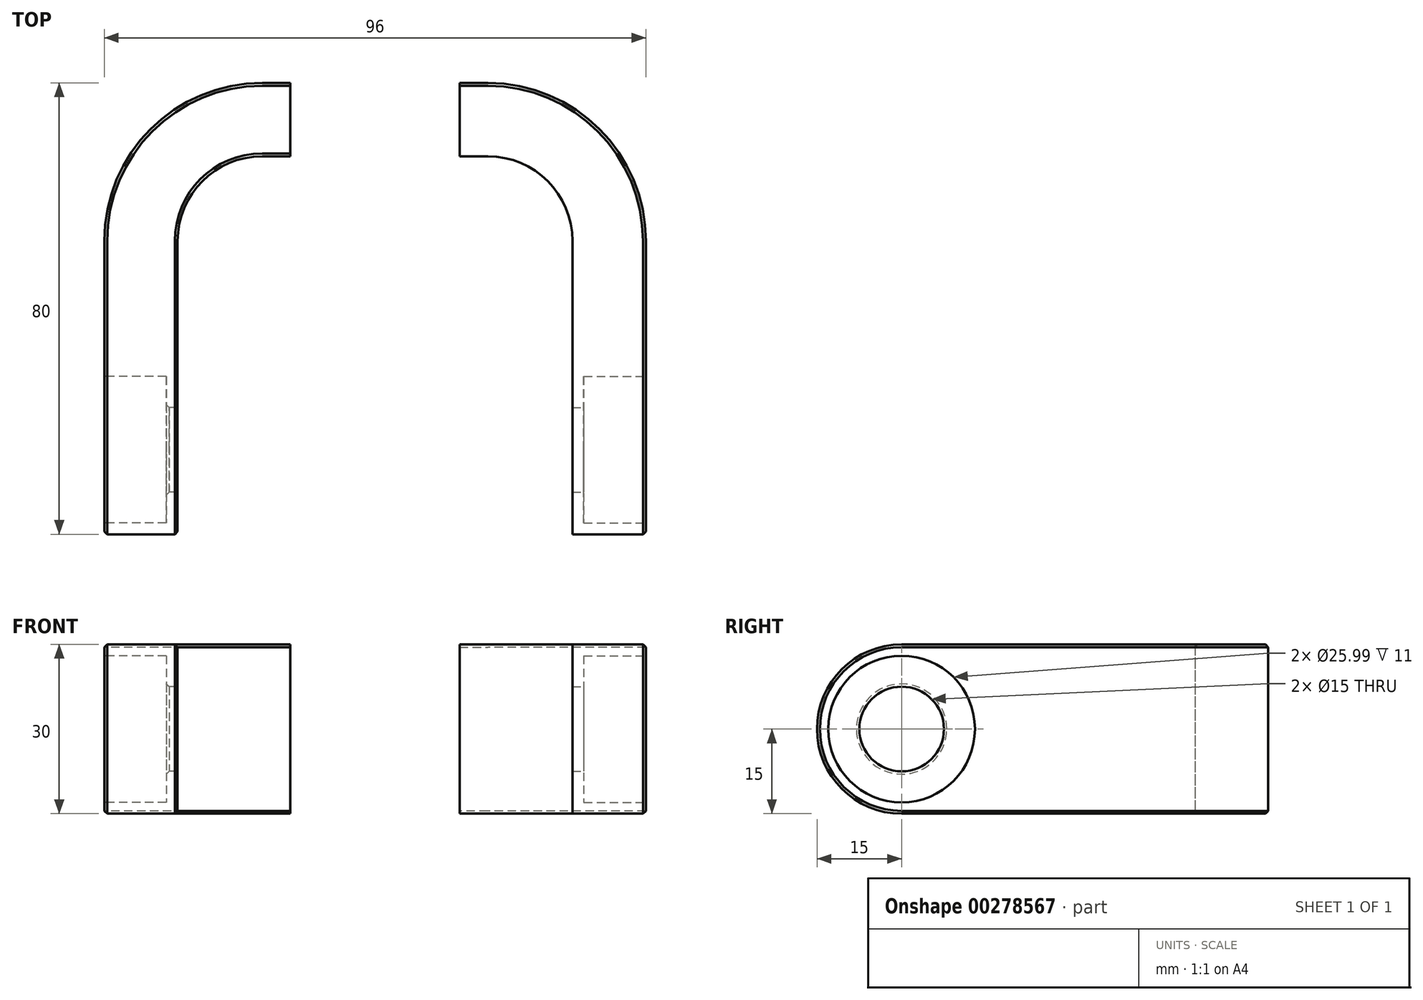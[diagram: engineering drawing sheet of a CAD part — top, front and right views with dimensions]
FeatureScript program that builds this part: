
annotation { "Feature Type Name" : "Feature", "Feature Type Description" : "" }
export const myFeature = defineFeature(function(context is Context, id is Id, definition is map)
    precondition{}
    {
        {
            var Q0;
            Q0=qCreatedBy(makeId("Top.planeOp"),FACE);
            var sketch = newSketch(context, id + "F0", { "sketchPlane" : qUnion([Q0])});
            skLineSegment(sketch, "E0.bottom", {"start": v(35, -52) * mm, "end": v(-35, -52) * mm});
            skLineSegment(sketch, "E0.top", {"start": v(35, 52) * mm, "end": v(-35, 52) * mm});
            skLineSegment(sketch, "E0.left", {"start": v(35, -52) * mm, "end": v(35, 52) * mm});
            skLineSegment(sketch, "E0.right", {"start": v(-35, -52) * mm, "end": v(-35, 52) * mm});
            skPoint(sketch, "E0.middle", {"position": v(0, 0) * mm});
            skLineSegment(sketch, "E1.bottom", {"start": v(48, -65) * mm, "end": v(-48, -65) * mm});
            skLineSegment(sketch, "E1.top", {"start": v(48, 65) * mm, "end": v(-48, 65) * mm});
            skLineSegment(sketch, "E1.left", {"start": v(48, -65) * mm, "end": v(48, 65) * mm});
            skLineSegment(sketch, "E1.right", {"start": v(-48, -65) * mm, "end": v(-48, 65) * mm});
            skLineSegment(sketch, "E2", {"start": v(-48, 0) * mm, "end": v(0, 0) * mm, "construction": true});
            skLineSegment(sketch, "E3", {"start": v(48, 0) * mm, "end": v(0, 0) * mm, "construction": true});
            skLineSegment(sketch, "E4", {"start": v(0, 65) * mm, "end": v(0, -65) * mm, "construction": true});
            skLineSegment(sketch, "E5.bottom", {"start": v(-35, 15) * mm, "end": v(-48, 15) * mm});
            skLineSegment(sketch, "E5.top", {"start": v(-35, -15) * mm, "end": v(-48, -15) * mm});
            skLineSegment(sketch, "E5.left", {"start": v(-35, 15) * mm, "end": v(-35, -15) * mm});
            skLineSegment(sketch, "E5.right", {"start": v(-48, 15) * mm, "end": v(-48, -15) * mm});
            skPoint(sketch, "E5.middle", {"position": v(-41.5, 0) * mm});
            skLineSegment(sketch, "E6.bottom", {"start": v(48, 15) * mm, "end": v(35, 15) * mm});
            skLineSegment(sketch, "E6.top", {"start": v(48, -15) * mm, "end": v(35, -15) * mm});
            skLineSegment(sketch, "E6.left", {"start": v(48, 15) * mm, "end": v(48, -15) * mm});
            skLineSegment(sketch, "E6.right", {"start": v(35, 15) * mm, "end": v(35, -15) * mm});
            skPoint(sketch, "E6.middle", {"position": v(41.5, 0) * mm});
            skLineSegment(sketch, "E7.bottom", {"start": v(15, 65) * mm, "end": v(-15, 65) * mm});
            skLineSegment(sketch, "E7.top", {"start": v(15, 52) * mm, "end": v(-15, 52) * mm});
            skLineSegment(sketch, "E7.left", {"start": v(15, 65) * mm, "end": v(15, 52) * mm});
            skLineSegment(sketch, "E7.right", {"start": v(-15, 65) * mm, "end": v(-15, 52) * mm});
            skPoint(sketch, "E7.middle", {"position": v(0, 58.5) * mm});
            skSolve(sketch);
        }
        {
            var Q0;
            Q0=makeQuery(id+"F0.imprint","IMPRINT",FACE,{"disambiguationData":[TD([[makeQuery(id+"F0.imprint","IMPRINT",EDGE,{"derivedFrom":sQuery(id+"F0.wireOp",EDGE,"E7.bottom")}),1.0]])]});
            var Q1;
            {var subQ3=sQuery(id+"F0.wireOp",EDGE,"E5.bottom");Q1=makeQuery(id+"F0.imprint","IMPRINT",FACE,{"disambiguationData":[TD([[makeQuery(id+"F0.imprint","IMPRINT",EDGE,{"derivedFrom":subQ3}),-1.0]])]});}
            var Q2;
            Q2=makeQuery(id+"F0.imprint","IMPRINT",FACE,{"disambiguationData":[TD([[makeQuery(id+"F0.imprint","IMPRINT",EDGE,{"derivedFrom":sQuery(id+"F0.wireOp",EDGE,"E5.bottom")}),1.0]])]});
            var Q3;
            {var subQ7=sQuery(id+"F0.wireOp",EDGE,"E6.bottom");Q3=makeQuery(id+"F0.imprint","IMPRINT",FACE,{"disambiguationData":[TD([[makeQuery(id+"F0.imprint","IMPRINT",EDGE,{"derivedFrom":subQ7}),-1.0]])]});}
            var Q4;
            Q4=makeQuery(id+"F0.imprint","IMPRINT",FACE,{"disambiguationData":[TD([[makeQuery(id+"F0.imprint","IMPRINT",EDGE,{"derivedFrom":sQuery(id+"F0.wireOp",EDGE,"E6.bottom")}),1.0]])]});
            extrude(context, id + "F1", {"entities" : qUnion([Q0, Q1, Q2, Q3, Q4]), "depth" : 15 * mm, "hasSecondDirection" : true, "secondDirectionOppositeDirection" : true, "secondDirectionDepth" : 15 * mm});
        }
        {
            var Q0;
            Q0=makeQuery(id+"F1.opExtrude","CAP_EDGE",EDGE,{"disambiguationData":[OSD([sQuery(id+"F0.wireOp",EDGE,"E5.top")])],"isStart":false});
            var Q1;
            Q1=makeQuery(id+"F1.opExtrude","CAP_EDGE",EDGE,{"disambiguationData":[OSD([sQuery(id+"F0.wireOp",EDGE,"E5.top")])],"isStart":true});
            var Q2;
            Q2=makeQuery(id+"F1.opExtrude","CAP_EDGE",EDGE,{"disambiguationData":[OSD([sQuery(id+"F0.wireOp",EDGE,"E6.top")])],"isStart":false});
            var Q3;
            Q3=makeQuery(id+"F1.opExtrude","CAP_EDGE",EDGE,{"disambiguationData":[OSD([sQuery(id+"F0.wireOp",EDGE,"E6.top")])],"isStart":true});
            var Q4;
            Q4=makeQuery(id+"F1.opExtrude","SWEPT_EDGE",EDGE,{"disambiguationData":[OSD([sQuery(id+"F0.wireOp",EDGE,"E0.top"),sQuery(id+"F0.wireOp",EDGE,"E0.right")])]});
            var Q5;
            Q5=makeQuery(id+"F1.opExtrude","SWEPT_EDGE",EDGE,{"disambiguationData":[OSD([sQuery(id+"F0.wireOp",EDGE,"E0.top"),sQuery(id+"F0.wireOp",EDGE,"E0.left")])]});
            var Q6;
            Q6=makeQuery(id+"FhP4Di1fzt5Cq4O_0.boolean.opBoolean","COPY",FACE,{"derivedFrom":makeQuery(id+"FhP4Di1fzt5Cq4O_0.opExtrude","SWEPT_FACE",FACE,{"disambiguationData":[OSD([sQuery(id+"F0.wireOp",EDGE,"E7.right")])]})});
            var Q7;
            Q7=makeQuery(id+"FhP4Di1fzt5Cq4O_0.boolean.opBoolean","COPY",EDGE,{"derivedFrom":makeQuery(id+"FhP4Di1fzt5Cq4O_0.opExtrude","CAP_EDGE",EDGE,{"disambiguationData":[OSD([sQuery(id+"F0.wireOp",EDGE,"E7.right")])],"isStart":false})});
            fillet(context, id + "F2", {"entities" : qUnion([Q0, Q1, Q2, Q3, Q4, Q5, Q6, Q7]), "radius" : 15 * mm, "tangentPropagation" : true, "allowEdgeOverflow" : false});
        }
        {
            var Q0;
            Q0=makeQuery(id+"F1.opExtrude","SWEPT_EDGE",EDGE,{"disambiguationData":[OSD([sQuery(id+"F0.wireOp",EDGE,"E1.top"),sQuery(id+"F0.wireOp",EDGE,"E1.left")])]});
            var Q1;
            Q1=makeQuery(id+"F1.opExtrude","SWEPT_EDGE",EDGE,{"disambiguationData":[OSD([sQuery(id+"F0.wireOp",EDGE,"E1.top"),sQuery(id+"F0.wireOp",EDGE,"E1.right")])]});
            fillet(context, id + "F3", {"entities" : qUnion([Q0, Q1]), "radius" : 28 * mm, "tangentPropagation" : true, "allowEdgeOverflow" : false});
        }
        {
            var Q0;
            Q0=makeQuery(id+"F1.opExtrude","SWEPT_FACE",FACE,{"disambiguationData":[OSD([sQuery(id+"F0.wireOp",EDGE,"E1.right"),sQuery(id+"F0.wireOp",EDGE,"E5.right")])]});
            var sketch = newSketch(context, id + "F4", { "sketchPlane" : qUnion([Q0])});
            skCircle(sketch, "E8", {"center": v(0, 0) * mm, "radius": 13 * mm});
            skCircle(sketch, "E9", {"center": v(0, 0) * mm, "radius": 7.5 * mm});
            skSolve(sketch);
        }
        {
            var Q0;
            Q0=makeQuery(id+"F4.imprint","IMPRINT",FACE,{"disambiguationData":[TD([[makeQuery(id+"F4.imprint","IMPRINT",EDGE,{"derivedFrom":sQuery(id+"F4.wireOp",EDGE,"E8")}),1.0]])]});
            var Q1;
            Q1=makeQuery(id+"F4.imprint","IMPRINT",FACE,{"disambiguationData":[TD([[makeQuery(id+"F4.imprint","IMPRINT",EDGE,{"derivedFrom":sQuery(id+"F4.wireOp",EDGE,"E9")}),1.0]])]});
            extrude(context, id + "F5", {"entities" : qUnion([Q0, Q1]), "operationType" : NewBodyOperationType.REMOVE, "oppositeDirection" : true, "depth" : 11 * mm});
        }
        {
            var Q0;
            Q0=makeQuery(id+"F4.imprint","IMPRINT",FACE,{"disambiguationData":[TD([[makeQuery(id+"F4.imprint","IMPRINT",EDGE,{"derivedFrom":sQuery(id+"F4.wireOp",EDGE,"E9")}),1.0]])]});
            var Q1;
            Q1=sQuery(id+"F4.wireOp",EDGE,"E9");
            extrude(context, id + "F6", {"entities" : qUnion([Q0]), "operationType" : NewBodyOperationType.REMOVE, "surfaceEntities" : qUnion([Q1]), "oppositeDirection" : true, "depth" : 13 * mm});
        }
        {
            var Q0;
            Q0=makeQuery(id+"F1.opExtrude","SWEPT_FACE",FACE,{"disambiguationData":[OSD([sQuery(id+"F0.wireOp",EDGE,"E1.top"),sQuery(id+"F0.wireOp",EDGE,"E7.bottom")])]});
            var sketch = newSketch(context, id + "F7", { "sketchPlane" : qUnion([Q0])});
            skCircle(sketch, "E10", {"center": v(0, 0) * mm, "radius": 13 * mm});
            skCircle(sketch, "E11", {"center": v(0, 0) * mm, "radius": 7.5 * mm});
            skCircle(sketch, "E12", {"center": v(0, 0) * mm, "radius": 14 * mm});
            skSolve(sketch);
        }
        {
            var Q0;
            Q0=makeQuery(id+"F7.imprint","IMPRINT",FACE,{"disambiguationData":[TD([[makeQuery(id+"F7.imprint","IMPRINT",EDGE,{"derivedFrom":sQuery(id+"F7.wireOp",EDGE,"E10")}),1.0]])]});
            var Q1;
            Q1=makeQuery(id+"F7.imprint","IMPRINT",FACE,{"disambiguationData":[TD([[makeQuery(id+"F7.imprint","IMPRINT",EDGE,{"derivedFrom":sQuery(id+"F7.wireOp",EDGE,"E11")}),1.0]])]});
            extrude(context, id + "F8", {"entities" : qUnion([Q0, Q1]), "operationType" : NewBodyOperationType.REMOVE, "oppositeDirection" : true, "depth" : 11 * mm});
        }
        {
            var Q0;
            Q0=makeQuery(id+"F7.imprint","IMPRINT",FACE,{"disambiguationData":[TD([[makeQuery(id+"F7.imprint","IMPRINT",EDGE,{"derivedFrom":sQuery(id+"F7.wireOp",EDGE,"E11")}),1.0]])]});
            extrude(context, id + "F9", {"entities" : qUnion([Q0]), "operationType" : NewBodyOperationType.REMOVE, "oppositeDirection" : true, "depth" : 13 * mm});
        }
        {
            var Q0;
            Q0=makeQuery(id+"F7.imprint","IMPRINT",FACE,{"disambiguationData":[TD([[makeQuery(id+"F7.imprint","IMPRINT",EDGE,{"derivedFrom":sQuery(id+"F7.wireOp",EDGE,"E10")}),-1.0]])]});
            extrude(context, id + "F10", {"entities" : qUnion([Q0]), "operationType" : NewBodyOperationType.REMOVE, "oppositeDirection" : true, "offsetDistance" : 25 * mm, "depth" : 3 * mm, "hasSecondDirection" : true, "secondDirectionOppositeDirection" : true, "secondDirectionDepth" : 1.7 * mm});
        }
        {
            var Q0;
            Q0=makeQuery(id+"F1.opExtrude","SWEPT_BODY",BODY,{"disambiguationData":[OSD([sQuery(id+"F0.wireOp",EDGE,"E0.top"),sQuery(id+"F0.wireOp",EDGE,"E0.left"),sQuery(id+"F0.wireOp",EDGE,"E0.right"),sQuery(id+"F0.wireOp",EDGE,"E1.top"),sQuery(id+"F0.wireOp",EDGE,"E1.left"),sQuery(id+"F0.wireOp",EDGE,"E1.right"),sQuery(id+"F0.wireOp",EDGE,"E5.top"),sQuery(id+"F0.wireOp",EDGE,"E5.left"),sQuery(id+"F0.wireOp",EDGE,"E5.right"),sQuery(id+"F0.wireOp",EDGE,"E6.top"),sQuery(id+"F0.wireOp",EDGE,"E6.left"),sQuery(id+"F0.wireOp",EDGE,"E6.right"),sQuery(id+"F0.wireOp",EDGE,"E7.bottom"),sQuery(id+"F0.wireOp",EDGE,"E7.top")])]});
            var Q1;
            Q1=qCreatedBy(makeId("Right.planeOp"),FACE);
            mirror(context, id + "F11", {"operationType" : NewBodyOperationType.INTERSECT, "entities" : qUnion([Q0]), "mirrorPlane" : qUnion([Q1])});
        }
        {
            var Q0;
            {var subQ0=sQuery(id+"F0.wireOp",EDGE,"E0.right");var subQ1=sQuery(id+"F0.wireOp",EDGE,"E0.top");Q0=makeQuery(id+"F2.opFillet","BLEND_EDGE",EDGE,{"blendedFrom":[makeQuery(id+"F1.opExtrude","SWEPT_EDGE",EDGE,{"disambiguationData":[OSD([subQ1,subQ0])]}),makeQuery(id+"F1.opExtrude","CAP_FACE",FACE,{"disambiguationData":[OSD([subQ1,sQuery(id+"F0.wireOp",EDGE,"E0.left"),subQ0,sQuery(id+"F0.wireOp",EDGE,"E1.top"),sQuery(id+"F0.wireOp",EDGE,"E1.left"),sQuery(id+"F0.wireOp",EDGE,"E1.right"),sQuery(id+"F0.wireOp",EDGE,"E5.top"),sQuery(id+"F0.wireOp",EDGE,"E5.left"),sQuery(id+"F0.wireOp",EDGE,"E5.right"),sQuery(id+"F0.wireOp",EDGE,"E6.top"),sQuery(id+"F0.wireOp",EDGE,"E6.left"),sQuery(id+"F0.wireOp",EDGE,"E6.right"),sQuery(id+"F0.wireOp",EDGE,"E7.bottom"),sQuery(id+"F0.wireOp",EDGE,"E7.top")])],"isStart":false})],"blendedInto":[makeQuery(id+"F1.opExtrude","CAP_FACE",FACE,{"disambiguationData":[OSD([subQ1,sQuery(id+"F0.wireOp",EDGE,"E0.left"),subQ0,sQuery(id+"F0.wireOp",EDGE,"E1.top"),sQuery(id+"F0.wireOp",EDGE,"E1.left"),sQuery(id+"F0.wireOp",EDGE,"E1.right"),sQuery(id+"F0.wireOp",EDGE,"E5.top"),sQuery(id+"F0.wireOp",EDGE,"E5.left"),sQuery(id+"F0.wireOp",EDGE,"E5.right"),sQuery(id+"F0.wireOp",EDGE,"E6.top"),sQuery(id+"F0.wireOp",EDGE,"E6.left"),sQuery(id+"F0.wireOp",EDGE,"E6.right"),sQuery(id+"F0.wireOp",EDGE,"E7.bottom"),sQuery(id+"F0.wireOp",EDGE,"E7.top")])],"isStart":false})]});}
            var Q1;
            Q1=makeQuery(id+"F1.opExtrude","CAP_EDGE",EDGE,{"disambiguationData":[OSD([sQuery(id+"F0.wireOp",EDGE,"E1.top"),sQuery(id+"F0.wireOp",EDGE,"E7.bottom")])],"isStart":true});
            var Q2;
            Q2=makeQuery(id+"F5.boolean.opBoolean","COPY",EDGE,{"derivedFrom":makeQuery(id+"F5.opExtrude","CAP_EDGE",EDGE,{"disambiguationData":[OSD([sQuery(id+"F4.wireOp",EDGE,"E8")])],"isStart":true})});
            var Q3;
            Q3=makeQuery(id+"F6.boolean.opBoolean","INTERSECT",EDGE,{"derivedFrom":[makeQuery(id+"F5.boolean.opBoolean","COPY",FACE,{"derivedFrom":makeQuery(id+"F5.opExtrude","CAP_FACE",FACE,{"disambiguationData":[OSD([sQuery(id+"F4.wireOp",EDGE,"E8")])],"isStart":false})}),makeQuery(id+"F6.opExtrude","SWEPT_FACE",FACE,{"disambiguationData":[OSD([sQuery(id+"F4.wireOp",EDGE,"E9")])]})]});
            var Q4;
            Q4=makeQuery(id+"F11.boolean.opBoolean","COPY",EDGE,{"derivedFrom":makeQuery(id+"F11.boolean.toolComplement.opBoolean","COPY",EDGE,{"derivedFrom":makeQuery(id+"F11.opPattern","COPY",EDGE,{"derivedFrom":makeQuery(id+"F5.boolean.opBoolean","COPY",EDGE,{"derivedFrom":makeQuery(id+"F5.opExtrude","CAP_EDGE",EDGE,{"disambiguationData":[OSD([sQuery(id+"F4.wireOp",EDGE,"E8")])],"isStart":true})}),"instanceName":"1"})})});
            var Q5;
            Q5=makeQuery(id+"F11.boolean.opBoolean","COPY",EDGE,{"derivedFrom":makeQuery(id+"F11.boolean.toolComplement.opBoolean","COPY",EDGE,{"derivedFrom":makeQuery(id+"F11.opPattern","COPY",EDGE,{"derivedFrom":makeQuery(id+"F6.boolean.opBoolean","INTERSECT",EDGE,{"derivedFrom":[makeQuery(id+"F5.boolean.opBoolean","COPY",FACE,{"derivedFrom":makeQuery(id+"F5.opExtrude","CAP_FACE",FACE,{"disambiguationData":[OSD([sQuery(id+"F4.wireOp",EDGE,"E8")])],"isStart":false})}),makeQuery(id+"F6.opExtrude","SWEPT_FACE",FACE,{"disambiguationData":[OSD([sQuery(id+"F4.wireOp",EDGE,"E9")])]})]}),"instanceName":"1"})})});
            var Q6;
            Q6=makeQuery(id+"F8.boolean.opBoolean","COPY",EDGE,{"derivedFrom":makeQuery(id+"F8.opExtrude","CAP_EDGE",EDGE,{"disambiguationData":[OSD([sQuery(id+"F7.wireOp",EDGE,"E10")])],"isStart":true})});
            var Q7;
            Q7=makeQuery(id+"F9.boolean.opBoolean","INTERSECT",EDGE,{"derivedFrom":[makeQuery(id+"F8.boolean.opBoolean","COPY",FACE,{"derivedFrom":makeQuery(id+"F8.opExtrude","CAP_FACE",FACE,{"disambiguationData":[OSD([sQuery(id+"F7.wireOp",EDGE,"E10")])],"isStart":false})}),makeQuery(id+"F9.opExtrude","SWEPT_FACE",FACE,{"disambiguationData":[OSD([sQuery(id+"F7.wireOp",EDGE,"E11")])]})]});
            chamfer(context, id + "F12", {"entities" : qUnion([Q0, Q1, Q2, Q3, Q4, Q5, Q6, Q7]), "width" : 0.5 * mm, "tangentPropagation" : true});
        }
    });
